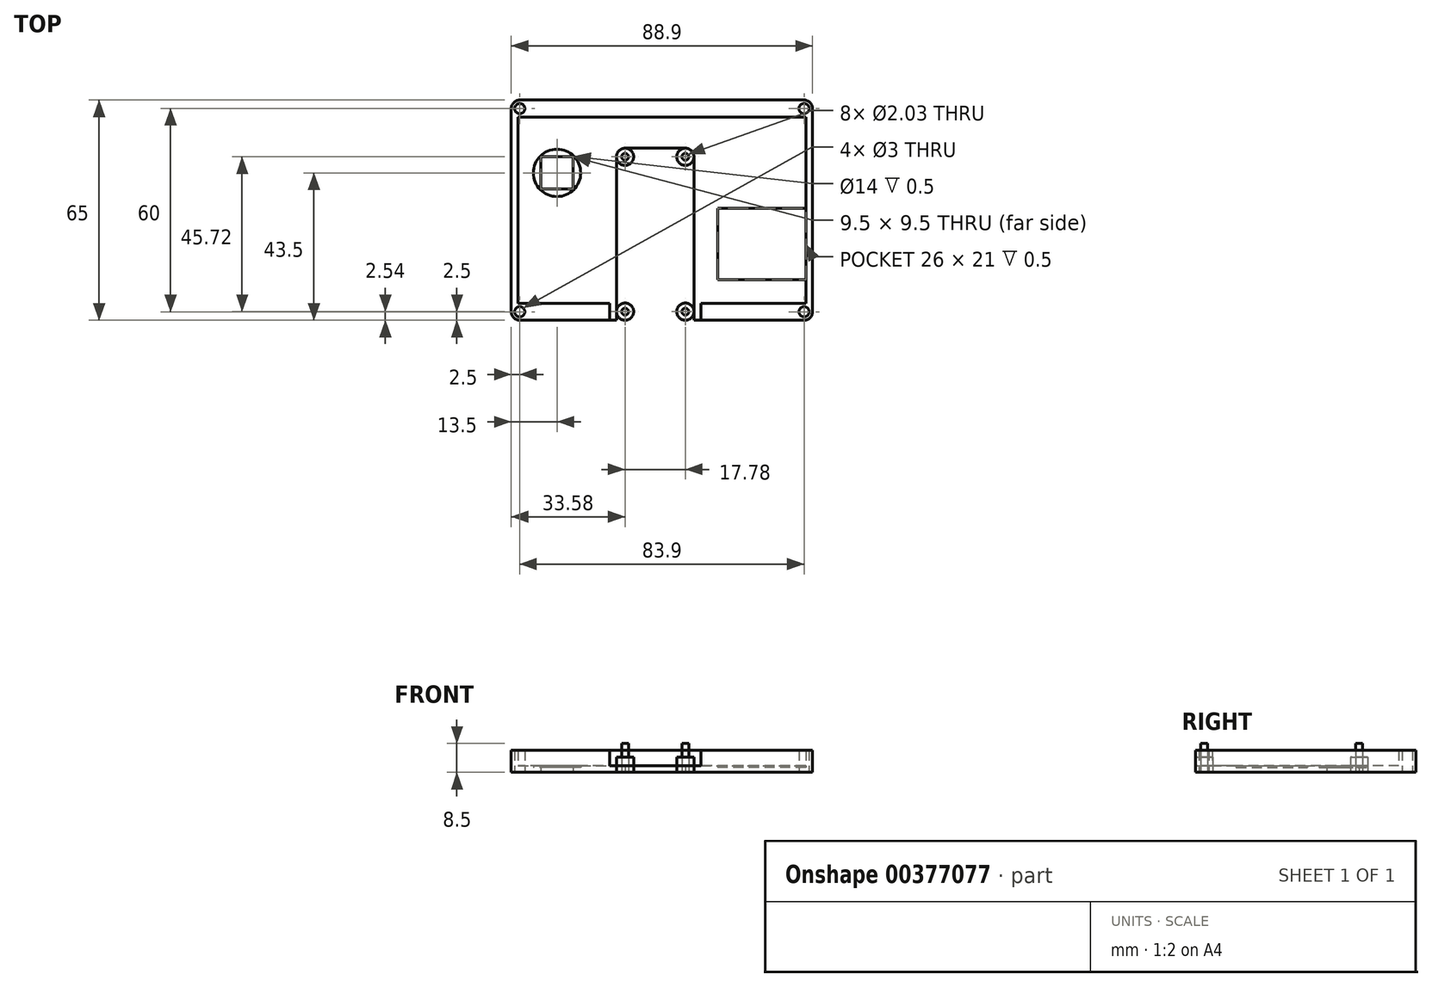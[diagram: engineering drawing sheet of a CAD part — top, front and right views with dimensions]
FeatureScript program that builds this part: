
annotation { "Feature Type Name" : "Feature", "Feature Type Description" : "" }
export const myFeature = defineFeature(function(context is Context, id is Id, definition is map)
    precondition{}
    {
        {
            var Q0;
            Q0=qCreatedBy(makeId("Top.planeOp"),FACE);
            var sketch = newSketch(context, id + "F0", { "sketchPlane" : qUnion([Q0])});
            skLineSegment(sketch, "E0.top", {"start": v(42.45, 27.5) * mm, "end": v(-42.45, 27.5) * mm});
            skLineSegment(sketch, "E0.left", {"start": v(44.45, -27.5) * mm, "end": v(44.45, 27.5) * mm});
            skLineSegment(sketch, "E0.right", {"start": v(-44.45, -27.5) * mm, "end": v(-44.45, 27.5) * mm});
            skPoint(sketch, "E0.middle", {"position": v(0, 0) * mm});
            skPoint(sketch, "E1", {"position": v(-30.95, 11) * mm});
            skLineSegment(sketch, "E2.bottom", {"start": v(-26.2, 6.25) * mm, "end": v(-35.7, 6.25) * mm});
            skLineSegment(sketch, "E2.top", {"start": v(-26.2, 15.75) * mm, "end": v(-35.7, 15.75) * mm});
            skLineSegment(sketch, "E2.left", {"start": v(-26.2, 6.25) * mm, "end": v(-26.2, 15.75) * mm});
            skLineSegment(sketch, "E2.right", {"start": v(-35.7, 6.25) * mm, "end": v(-35.7, 15.75) * mm});
            skCircle(sketch, "E3", {"center": v(-30.95, 11) * mm, "radius": 7 * mm});
            skLineSegment(sketch, "E4", {"start": v(42.45, 31.41) * mm, "end": v(42.45, 31.27) * mm, "construction": true});
            skLineSegment(sketch, "E5.bottom", {"start": v(42.45, -20.5) * mm, "end": v(16.45, -20.5) * mm});
            skLineSegment(sketch, "E5.top", {"start": v(42.45, 0.5) * mm, "end": v(16.45, 0.5) * mm});
            skLineSegment(sketch, "E5.left", {"start": v(42.45, -20.5) * mm, "end": v(42.45, 0.5) * mm});
            skLineSegment(sketch, "E5.right", {"start": v(16.45, -20.5) * mm, "end": v(16.45, 0.5) * mm});
            skLineSegment(sketch, "E6.bottom", {"start": v(-42.45, 27.5) * mm, "end": v(42.45, 27.5) * mm});
            skLineSegment(sketch, "E6.top", {"start": v(-41.95, 32.5) * mm, "end": v(41.95, 32.5) * mm});
            skLineSegment(sketch, "E6.left", {"start": v(-44.45, 27.5) * mm, "end": v(-44.45, 30) * mm});
            skLineSegment(sketch, "E6.right", {"start": v(44.45, 27.5) * mm, "end": v(44.45, 30) * mm});
            skLineSegment(sketch, "E7.top", {"start": v(-41.95, -32.5) * mm, "end": v(41.95, -32.5) * mm});
            skLineSegment(sketch, "E7.left", {"start": v(-44.45, -27.5) * mm, "end": v(-44.45, -30) * mm});
            skLineSegment(sketch, "E7.right", {"start": v(44.45, -27.5) * mm, "end": v(44.45, -30) * mm});
            skPoint(sketch, "E8.visualSharp", {"position": v(-44.45, 32.5) * mm});
            skArc(sketch, "E8.filletArc", {"start": v(-41.95, 32.5) * mm, "mid": v(-43.72, 31.77) * mm, "end": v(-44.45, 30) * mm});
            skPoint(sketch, "E9.visualSharp", {"position": v(44.45, 32.5) * mm});
            skArc(sketch, "E9.filletArc", {"start": v(44.45, 30) * mm, "mid": v(43.72, 31.77) * mm, "end": v(41.95, 32.5) * mm});
            skPoint(sketch, "E10.visualSharp", {"position": v(44.45, -32.5) * mm});
            skArc(sketch, "E10.filletArc", {"start": v(41.95, -32.5) * mm, "mid": v(43.72, -31.77) * mm, "end": v(44.45, -30) * mm});
            skPoint(sketch, "E11.visualSharp", {"position": v(-44.45, -32.5) * mm});
            skArc(sketch, "E11.filletArc", {"start": v(-44.45, -30) * mm, "mid": v(-43.72, -31.77) * mm, "end": v(-41.95, -32.5) * mm});
            skCircle(sketch, "E12", {"center": v(-41.95, 30) * mm, "radius": 1.5 * mm});
            skCircle(sketch, "E13", {"center": v(41.95, 30) * mm, "radius": 1.5 * mm});
            skCircle(sketch, "E14", {"center": v(-41.95, -30) * mm, "radius": 1.5 * mm});
            skCircle(sketch, "E15", {"center": v(41.95, -30) * mm, "radius": 1.5 * mm});
            skLineSegment(sketch, "E16.trimOffspring", {"start": v(42.45, 0.5) * mm, "end": v(42.45, -20.5) * mm, "construction": true});
            skLineSegment(sketch, "E17.trimOffspring", {"start": v(42.45, -32.45) * mm, "end": v(42.45, -32.5) * mm, "construction": true});
            skPoint(sketch, "E0.bottom.end.orphan", {"position": v(9.45, -27.5) * mm});
            skLineSegment(sketch, "E18.bottom", {"start": v(-13.4, -32.5) * mm, "end": v(9.45, -32.5) * mm});
            skLineSegment(sketch, "E18.top", {"start": v(-13.41, 18.3) * mm, "end": v(9.45, 18.3) * mm});
            skLineSegment(sketch, "E18.left", {"start": v(-13.4, -32.5) * mm, "end": v(-13.41, 18.3) * mm});
            skLineSegment(sketch, "E18.right", {"start": v(9.45, -32.5) * mm, "end": v(9.45, 18.3) * mm});
            skLineSegment(sketch, "E19.0", {"start": v(6.91, -29.96) * mm, "end": v(6.9, 15.76) * mm, "construction": true});
            skLineSegment(sketch, "E19.1", {"start": v(-10.87, 15.76) * mm, "end": v(6.9, 15.76) * mm, "construction": true});
            skLineSegment(sketch, "E19.2", {"start": v(-10.87, -29.96) * mm, "end": v(-10.87, 15.76) * mm, "construction": true});
            skLineSegment(sketch, "E20", {"start": v(-10.87, -29.96) * mm, "end": v(6.91, -29.96) * mm, "construction": true});
            skCircle(sketch, "E21", {"center": v(-10.87, 15.76) * mm, "radius": 1.02 * mm});
            skCircle(sketch, "E22", {"center": v(6.9, 15.76) * mm, "radius": 1.02 * mm});
            skCircle(sketch, "E23", {"center": v(-10.87, -29.96) * mm, "radius": 1.02 * mm});
            skCircle(sketch, "E24", {"center": v(6.91, -29.96) * mm, "radius": 1.02 * mm});
            skLineSegment(sketch, "E25", {"start": v(-42.45, -27.5) * mm, "end": v(-15.4, -27.5) * mm});
            skLineSegment(sketch, "E26", {"start": v(11.45, -27.5) * mm, "end": v(42.45, -27.5) * mm});
            skLineSegment(sketch, "E27", {"start": v(42.45, 27.5) * mm, "end": v(42.45, -27.5) * mm});
            skLineSegment(sketch, "E28", {"start": v(-42.45, 27.5) * mm, "end": v(-42.45, -27.5) * mm});
            skCircle(sketch, "E29", {"center": v(-10.87, 15.76) * mm, "radius": 2.54 * mm});
            skCircle(sketch, "E30", {"center": v(6.9, 15.76) * mm, "radius": 2.54 * mm});
            skCircle(sketch, "E31", {"center": v(-10.87, -29.96) * mm, "radius": 2.54 * mm});
            skCircle(sketch, "E32", {"center": v(6.91, -29.96) * mm, "radius": 2.54 * mm});
            skLineSegment(sketch, "E33", {"start": v(-15.4, -27.5) * mm, "end": v(-15.4, -32.5) * mm});
            skLineSegment(sketch, "E34", {"start": v(11.45, -27.5) * mm, "end": v(11.45, -32.5) * mm});
            skSolve(sketch);
        }
        {
            var Q0;
            Q0=makeQuery(id+"F0.imprint","IMPRINT",FACE,{"disambiguationData":[TD([[makeQuery(id+"F0.imprint","IMPRINT",EDGE,{"derivedFrom":sQuery(id+"F0.wireOp",EDGE,"E23")}),1.0]])]});
            var Q1;
            Q1=makeQuery(id+"F0.imprint","IMPRINT",FACE,{"disambiguationData":[TD([[makeQuery(id+"F0.imprint","IMPRINT",EDGE,{"derivedFrom":sQuery(id+"F0.wireOp",EDGE,"E24")}),1.0]])]});
            var Q2;
            Q2=makeQuery(id+"F0.imprint","IMPRINT",FACE,{"disambiguationData":[TD([[makeQuery(id+"F0.imprint","IMPRINT",EDGE,{"derivedFrom":sQuery(id+"F0.wireOp",EDGE,"E21")}),1.0]])]});
            var Q3;
            Q3=makeQuery(id+"F0.imprint","IMPRINT",FACE,{"disambiguationData":[TD([[makeQuery(id+"F0.imprint","IMPRINT",EDGE,{"derivedFrom":sQuery(id+"F0.wireOp",EDGE,"E22")}),1.0]])]});
            var Q4;
            Q4=makeQuery(id+"F0.imprint","IMPRINT",FACE,{"disambiguationData":[TD([[makeQuery(id+"F0.imprint","IMPRINT",EDGE,{"derivedFrom":sQuery(id+"F0.wireOp",EDGE,"E0.left")}),1.0]])]});
            extrude(context, id + "F1", {"entities" : qUnion([Q0, Q1, Q2, Q3, Q4]), "depth" : 6.5 * mm});
        }
        {
            var Q0;
            Q0=makeQuery(id+"F0.imprint","IMPRINT",FACE,{"disambiguationData":[TD([[makeQuery(id+"F0.imprint","IMPRINT",EDGE,{"derivedFrom":sQuery(id+"F0.wireOp",EDGE,"E3")}),-1.0]])]});
            var Q1;
            {var subQ3=sQuery(id+"F0.wireOp",EDGE,"E18.bottom");Q1=makeQuery(id+"F0.imprint","IMPRINT",FACE,{"disambiguationData":[TD([[makeQuery(id+"F0.imprint","IMPRINT",EDGE,{"derivedFrom":subQ3}),1.0]])]});}
            var Q2;
            {var subQ5=sQuery(id+"F0.wireOp",EDGE,"E18.bottom");var subQ9=sQuery(id+"F0.wireOp",EDGE,"E31");var subQ11=makeQuery(id+"F0.imprint","INTERSECT",VERTEX,{"derivedFrom":[subQ5,subQ9]});Q2=makeQuery(id+"F0.imprint","IMPRINT",FACE,{"disambiguationData":[TD([[makeQuery(id+"F0.imprint","IMPRINT",EDGE,{"disambiguationData":[TD([[subQ11,-1.0]])],"derivedFrom":subQ5}),1.0]])]});}
            var Q3;
            {var subQ0=sQuery(id+"F0.wireOp",EDGE,"E18.right");var subQ1=sQuery(id+"F0.wireOp",EDGE,"E18.top");var subQ2=makeQuery(id+"F0.imprint","INTERSECT",VERTEX,{"derivedFrom":[subQ1,subQ0]});Q3=makeQuery(id+"F0.imprint","IMPRINT",FACE,{"disambiguationData":[TD([[makeQuery(id+"F0.imprint","IMPRINT",EDGE,{"disambiguationData":[TD([[subQ2,1.0]])],"derivedFrom":subQ1}),-1.0]])]});}
            var Q4;
            {var subQ0=sQuery(id+"F0.wireOp",EDGE,"E18.left");var subQ1=sQuery(id+"F0.wireOp",EDGE,"E18.top");var subQ2=makeQuery(id+"F0.imprint","INTERSECT",VERTEX,{"derivedFrom":[subQ1,subQ0]});Q4=makeQuery(id+"F0.imprint","IMPRINT",FACE,{"disambiguationData":[TD([[makeQuery(id+"F0.imprint","IMPRINT",EDGE,{"disambiguationData":[TD([[subQ2,-1.0]])],"derivedFrom":subQ1}),-1.0]])]});}
            var Q5;
            Q5=makeQuery(id+"F0.imprint","IMPRINT",FACE,{"disambiguationData":[TD([[makeQuery(id+"F0.imprint","IMPRINT",EDGE,{"derivedFrom":sQuery(id+"F0.wireOp",EDGE,"E22")}),-1.0]])]});
            var Q6;
            Q6=makeQuery(id+"F0.imprint","IMPRINT",FACE,{"disambiguationData":[TD([[makeQuery(id+"F0.imprint","IMPRINT",EDGE,{"derivedFrom":sQuery(id+"F0.wireOp",EDGE,"E23")}),-1.0]])]});
            var Q7;
            Q7=makeQuery(id+"F1.opExtrude","CAP_FACE",FACE,{"disambiguationData":[OSD([sQuery(id+"F0.wireOp",EDGE,"E23")])],"isStart":false});
            var Q8;
            Q8=makeQuery(id+"F0.imprint","IMPRINT",FACE,{"disambiguationData":[TD([[makeQuery(id+"F0.imprint","IMPRINT",EDGE,{"derivedFrom":sQuery(id+"F0.wireOp",EDGE,"E24")}),-1.0]])]});
            var Q9;
            Q9=makeQuery(id+"F1.opExtrude","CAP_FACE",FACE,{"disambiguationData":[OSD([sQuery(id+"F0.wireOp",EDGE,"E24")])],"isStart":false});
            var Q10;
            Q10=makeQuery(id+"F0.imprint","IMPRINT",FACE,{"disambiguationData":[TD([[makeQuery(id+"F0.imprint","IMPRINT",EDGE,{"derivedFrom":sQuery(id+"F0.wireOp",EDGE,"E21")}),-1.0]])]});
            var Q11;
            Q11=makeQuery(id+"F1.opExtrude","CAP_FACE",FACE,{"disambiguationData":[OSD([sQuery(id+"F0.wireOp",EDGE,"E21")])],"isStart":false});
            var Q12;
            Q12=makeQuery(id+"F1.opExtrude","CAP_FACE",FACE,{"disambiguationData":[OSD([sQuery(id+"F0.wireOp",EDGE,"E22")])],"isStart":false});
            extrude(context, id + "F2", {"entities" : qUnion([Q0, Q1, Q2, Q3, Q4, Q5, Q6, Q7, Q8, Q9, Q10, Q11, Q12]), "depth" : 2 * mm});
        }
        {
            var Q0;
            Q0=makeQuery(id+"F0.imprint","IMPRINT",FACE,{"disambiguationData":[TD([[makeQuery(id+"F0.imprint","IMPRINT",EDGE,{"derivedFrom":sQuery(id+"F0.wireOp",EDGE,"E2.bottom")}),1.0]])]});
            var Q1;
            {var subQ0=sQuery(id+"F0.wireOp",EDGE,"E5.bottom");Q1=makeQuery(id+"F0.imprint","IMPRINT",FACE,{"disambiguationData":[TD([[makeQuery(id+"F0.imprint","IMPRINT",EDGE,{"derivedFrom":subQ0}),-1.0]])]});}
            extrude(context, id + "F3", {"entities" : qUnion([Q0, Q1]), "operationType" : NewBodyOperationType.ADD, "depth" : 1.5 * mm});
        }
        {
            var Q0;
            Q0=makeQuery(id+"F0.imprint","IMPRINT",FACE,{"disambiguationData":[TD([[makeQuery(id+"F0.imprint","IMPRINT",EDGE,{"derivedFrom":sQuery(id+"F0.wireOp",EDGE,"E21")}),-1.0]])]});
            var Q1;
            Q1=makeQuery(id+"F0.imprint","IMPRINT",FACE,{"disambiguationData":[TD([[makeQuery(id+"F0.imprint","IMPRINT",EDGE,{"derivedFrom":sQuery(id+"F0.wireOp",EDGE,"E22")}),-1.0]])]});
            var Q2;
            Q2=makeQuery(id+"F0.imprint","IMPRINT",FACE,{"disambiguationData":[TD([[makeQuery(id+"F0.imprint","IMPRINT",EDGE,{"derivedFrom":sQuery(id+"F0.wireOp",EDGE,"E24")}),-1.0]])]});
            var Q3;
            Q3=makeQuery(id+"F0.imprint","IMPRINT",FACE,{"disambiguationData":[TD([[makeQuery(id+"F0.imprint","IMPRINT",EDGE,{"derivedFrom":sQuery(id+"F0.wireOp",EDGE,"E23")}),-1.0]])]});
            extrude(context, id + "F4", {"entities" : qUnion([Q0, Q1, Q2, Q3]), "depth" : 4.5 * mm});
        }
    });
